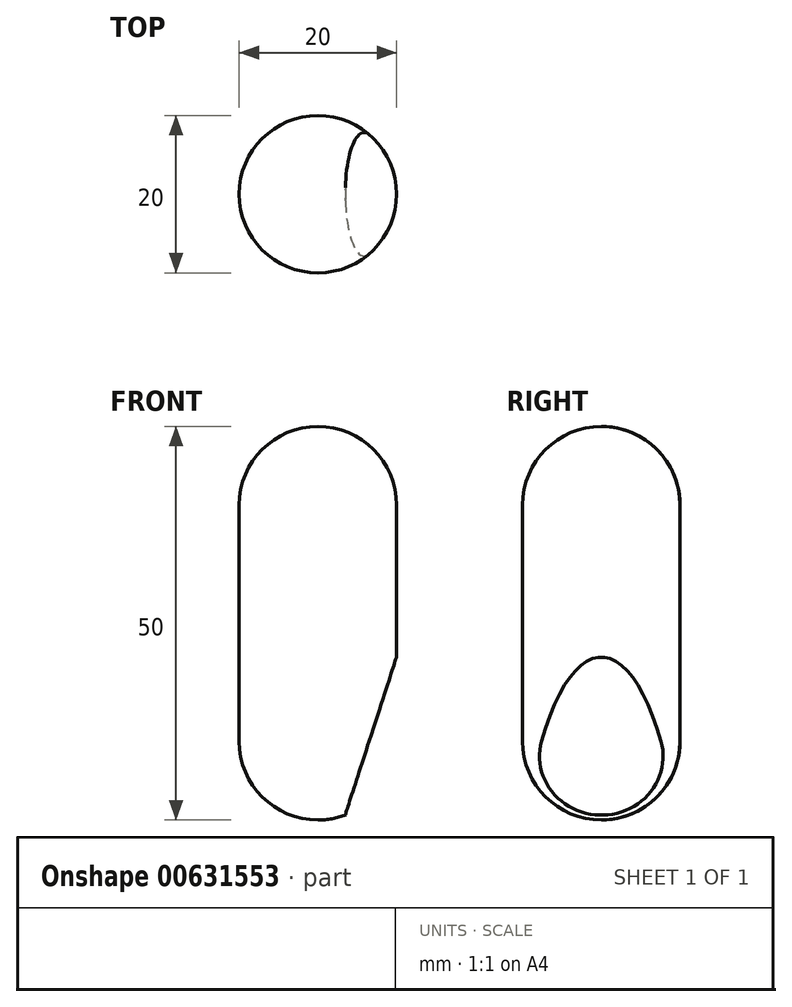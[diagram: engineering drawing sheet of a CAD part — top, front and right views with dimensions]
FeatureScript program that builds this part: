
annotation { "Feature Type Name" : "Feature", "Feature Type Description" : "" }
export const myFeature = defineFeature(function(context is Context, id is Id, definition is map)
    precondition{}
    {
        {
            var Q0;
            Q0=qCreatedBy(makeId("Right.planeOp"),FACE);
            var sketch = newSketch(context, id + "F0", { "sketchPlane" : qUnion([Q0])});
            skLineSegment(sketch, "E0.left", {"start": v(-142.83, 1.55) * mm, "end": v(-142.83, -28.45) * mm});
            skArc(sketch, "E1", {"start": v(-152.83, -8.45) * mm, "mid": v(-142.83, 1.55) * mm, "end": v(-152.83, 11.55) * mm});
            skPoint(sketch, "E1.first.point", {"position": v(-142.83, 1.55) * mm});
            skPoint(sketch, "E1.second.point", {"position": v(-152.83, 11.55) * mm});
            skArc(sketch, "E2", {"start": v(-152.83, -38.45) * mm, "mid": v(-142.83, -28.45) * mm, "end": v(-152.83, -18.45) * mm});
            skPoint(sketch, "E2.first.point", {"position": v(-143.11, -30.83) * mm});
            skPoint(sketch, "E2.second.point", {"position": v(-153.01, -38.44) * mm});
            skLineSegment(sketch, "E3", {"start": v(-152.83, 11.55) * mm, "end": v(-152.83, -38.45) * mm});
            skPoint(sketch, "E4.orphan", {"position": v(-142.83, 11.55) * mm});
            skPoint(sketch, "E5.orphan", {"position": v(-162.83, -38.45) * mm});
            skPoint(sketch, "E6.orphan", {"position": v(-142.83, -38.45) * mm});
            skSolve(sketch);
        }
        {
            var Q0;
            {var subQ0=sQuery(id+"F0.wireOp",EDGE,"E1");var subQ1=makeQuery(id+"F0.imprint","INTERSECT",VERTEX,{"derivedFrom":[sQuery(id+"F0.wireOp",EDGE,"E0.left"),subQ0]});Q0=makeQuery(id+"F0.imprint","IMPRINT",FACE,{"disambiguationData":[TD([[makeQuery(id+"F0.imprint","IMPRINT",EDGE,{"disambiguationData":[TD([[subQ1,1.0]])],"derivedFrom":subQ0}),1.0]])]});}
            var Q1;
            {var subQ0=sQuery(id+"F0.wireOp",EDGE,"E0.left");Q1=makeQuery(id+"F0.imprint","IMPRINT",FACE,{"disambiguationData":[TD([[makeQuery(id+"F0.imprint","IMPRINT",EDGE,{"derivedFrom":subQ0}),-1.0]])]});}
            var Q2;
            {var subQ0=sQuery(id+"F0.wireOp",EDGE,"E2");var subQ1=makeQuery(id+"F0.imprint","INTERSECT",VERTEX,{"derivedFrom":[sQuery(id+"F0.wireOp",EDGE,"E0.left"),subQ0]});Q2=makeQuery(id+"F0.imprint","IMPRINT",FACE,{"disambiguationData":[TD([[makeQuery(id+"F0.imprint","IMPRINT",EDGE,{"disambiguationData":[TD([[subQ1,1.0]])],"derivedFrom":subQ0}),1.0]])]});}
            var Q3;
            Q3=sQuery(id+"F0.wireOp",EDGE,"E3");
            revolve(context, id + "F1", {"entities" : qUnion([Q0, Q1, Q2]), "axis" : qUnion([Q3]), "revolveType" : RevolveType.FULL});
        }
        {
            var Q0;
            Q0=qCreatedBy(makeId("Front.planeOp"),FACE);
            var sketch = newSketch(context, id + "F2", { "sketchPlane" : qUnion([Q0])});
            skLineSegment(sketch, "E7", {"start": v(10, -28.35) * mm, "end": v(10, 18.82) * mm, "construction": true});
            skLineSegment(sketch, "E8", {"start": v(10, -17.7) * mm, "end": v(3.48, -37.79) * mm});
            skArc(sketch, "E9", {"start": v(10, -28.35) * mm, "mid": v(7.08, -35.45) * mm, "end": v(0, -38.44) * mm, "construction": true});
            skLineSegment(sketch, "E10", {"start": v(3.48, -37.79) * mm, "end": v(10, -37.79) * mm});
            skLineSegment(sketch, "E11", {"start": v(10, -37.79) * mm, "end": v(10, -17.7) * mm});
            skSolve(sketch);
        }
        {
            var Q0;
            Q0=makeQuery(id+"F2.imprint","IMPRINT",FACE,{"disambiguationData":[TD([[makeQuery(id+"F2.imprint","IMPRINT",EDGE,{"derivedFrom":sQuery(id+"F2.wireOp",EDGE,"E8")}),1.0]])]});
            var Q1;
            Q1=makeQuery(id+"F1.opRevolve","SWEPT_BODY",BODY,{"disambiguationData":[OSD([sQuery(id+"F0.wireOp",EDGE,"E0.left"),sQuery(id+"F0.wireOp",EDGE,"E1"),sQuery(id+"F0.wireOp",EDGE,"E2"),sQuery(id+"F0.wireOp",EDGE,"E3")])]});
            extrude(context, id + "F3", {"entities" : qUnion([Q0]), "oppositeDirection" : true, "depth" : 67 * mm, "endBoundEntityBody" : qUnion([Q1]), "offsetDistance" : 25 * mm});
        }
        {
            var Q0;
            Q0=makeQuery(id+"F1.opRevolve","SWEPT_BODY",BODY,{"disambiguationData":[OSD([sQuery(id+"F0.wireOp",EDGE,"E0.left"),sQuery(id+"F0.wireOp",EDGE,"E1"),sQuery(id+"F0.wireOp",EDGE,"E2"),sQuery(id+"F0.wireOp",EDGE,"E3")])]});
            var Q1;
            Q1=qCreatedBy(makeId("Origin.pointOp"),VERTEX);
            var Q2;
            Q2=qCreatedBy(makeId("Front.planeOp"),FACE);
            transform(context, id + "F4", {"entities" : qUnion([Q0]), "transformType" : TransformType.TRANSLATION_DISTANCE, "transformDirection" : qUnion([Q2]), "distance" : 154 * mm, "oppositeDirection" : true, "makeCopy" : false});
        }
        {
            var Q0;
            Q0=makeQuery(id+"F3.opExtrude","SWEPT_BODY",BODY,{"disambiguationData":[OSD([sQuery(id+"F2.wireOp",EDGE,"E8"),sQuery(id+"F2.wireOp",EDGE,"E10"),sQuery(id+"F2.wireOp",EDGE,"E11")])]});
            var Q1;
            Q1=sQuery(id+"F0.wireOp",EDGE,"E0.left");
            var Q2;
            Q2=qCreatedBy(makeId("Front.planeOp"),FACE);
            transform(context, id + "F5", {"entities" : qUnion([Q0]), "transformType" : TransformType.TRANSLATION_DISTANCE, "transformDirection" : qUnion([Q2]), "distance" : 25 * mm, "makeCopy" : false});
        }
        {
            var Q0;
            Q0=makeQuery(id+"F3.opExtrude","SWEPT_BODY",BODY,{"disambiguationData":[OSD([sQuery(id+"F2.wireOp",EDGE,"E8"),sQuery(id+"F2.wireOp",EDGE,"E10"),sQuery(id+"F2.wireOp",EDGE,"E11")])]});
            var Q1;
            Q1=makeQuery(id+"F1.opRevolve","SWEPT_BODY",BODY,{"disambiguationData":[OSD([sQuery(id+"F0.wireOp",EDGE,"E0.left"),sQuery(id+"F0.wireOp",EDGE,"E1"),sQuery(id+"F0.wireOp",EDGE,"E2"),sQuery(id+"F0.wireOp",EDGE,"E3")])]});
            booleanBodies(context, id + "F6", {"operationType" : BooleanOperationType.SUBTRACTION, "tools" : qUnion([Q0]), "targets" : qUnion([Q1])});
        }
    });
